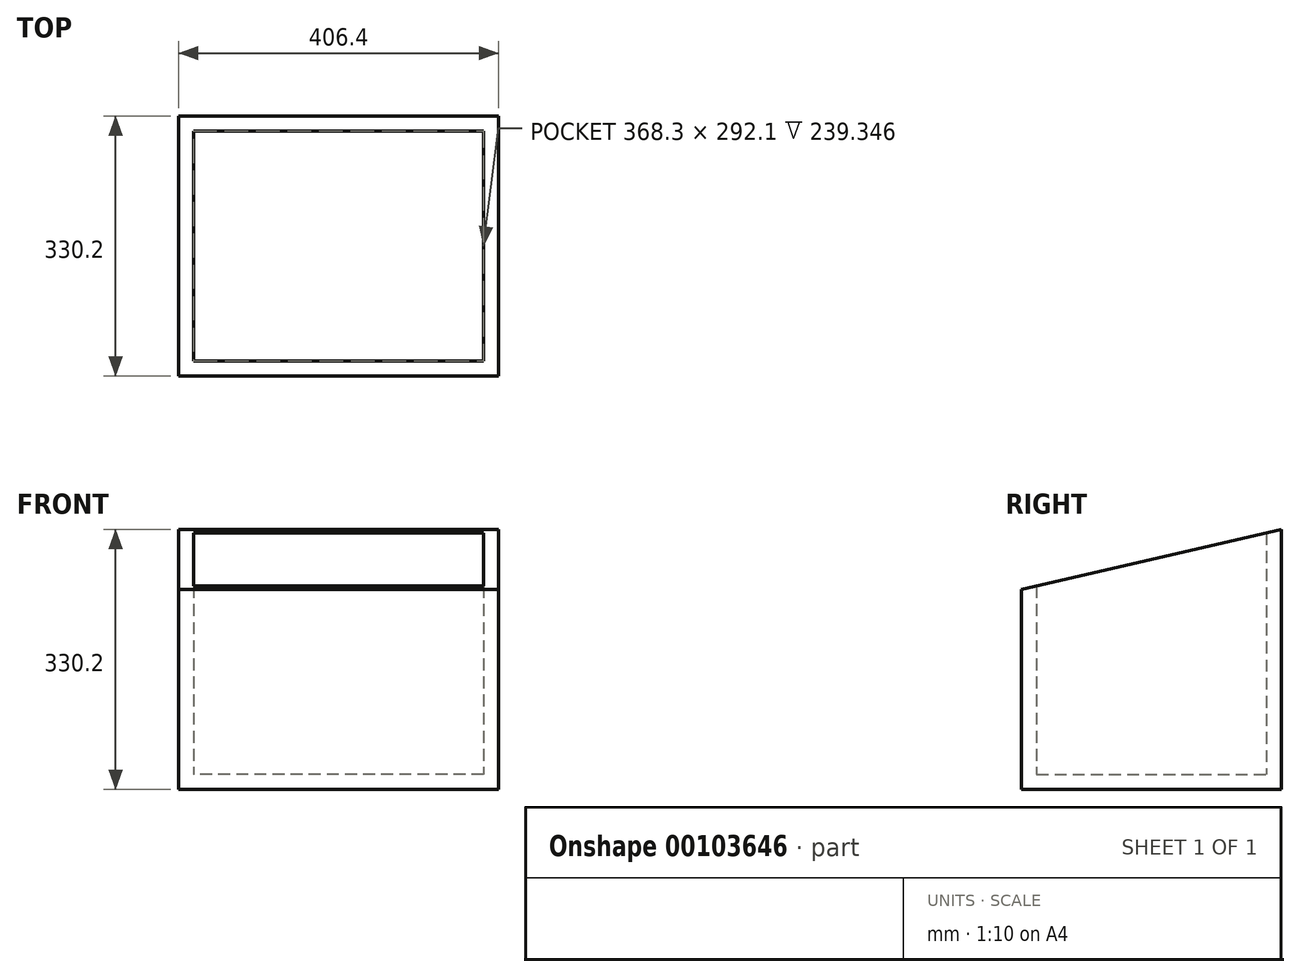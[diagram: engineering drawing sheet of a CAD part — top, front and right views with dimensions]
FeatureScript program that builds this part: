
annotation { "Feature Type Name" : "Feature", "Feature Type Description" : "" }
export const myFeature = defineFeature(function(context is Context, id is Id, definition is map)
    precondition{}
    {
        {
            var Q0;
            Q0=qCreatedBy(makeId("Front.planeOp"),FACE);
            var sketch = newSketch(context, id + "F0", { "sketchPlane" : qUnion([Q0])});
            skLineSegment(sketch, "E0.bottom", {"start": v(203.2, 165.1) * mm, "end": v(-203.2, 165.1) * mm});
            skLineSegment(sketch, "E0.top", {"start": v(203.2, -165.1) * mm, "end": v(-203.2, -165.1) * mm});
            skLineSegment(sketch, "E0.left", {"start": v(203.2, 165.1) * mm, "end": v(203.2, -165.1) * mm});
            skLineSegment(sketch, "E0.right", {"start": v(-203.2, 165.1) * mm, "end": v(-203.2, -165.1) * mm});
            skPoint(sketch, "E0.middle", {"position": v(0, 0) * mm});
            skSolve(sketch);
        }
        {
            var Q0;
            Q0=makeQuery(id+"F0.imprint","IMPRINT",FACE,{"disambiguationData":[TD([[makeQuery(id+"F0.imprint","IMPRINT",EDGE,{"derivedFrom":sQuery(id+"F0.wireOp",EDGE,"E0.bottom")}),1.0]])]});
            extrude(context, id + "F1", {"entities" : qUnion([Q0]), "endBound" : BoundingType.SYMMETRIC, "depth" : 330.2 * mm});
        }
        {
            var Q0;
            Q0=makeQuery(id+"F1.opExtrude","SWEPT_FACE",FACE,{"disambiguationData":[OSD([sQuery(id+"F0.wireOp",EDGE,"E0.left")])]});
            var sketch = newSketch(context, id + "F2", { "sketchPlane" : qUnion([Q0])});
            skLineSegment(sketch, "E1", {"start": v(-165.1, 165.1) * mm, "end": v(-165.1, 88.9) * mm});
            skLineSegment(sketch, "E2", {"start": v(-165.1, 88.9) * mm, "end": v(165.1, 165.1) * mm});
            skLineSegment(sketch, "E3", {"start": v(165.1, 165.1) * mm, "end": v(-165.1, 165.1) * mm});
            skSolve(sketch);
        }
        {
            var Q0;
            Q0=makeQuery(id+"F2.imprint","IMPRINT",FACE,{"disambiguationData":[TD([[makeQuery(id+"F2.imprint","IMPRINT",EDGE,{"derivedFrom":sQuery(id+"F2.wireOp",EDGE,"E1")}),1.0]])]});
            extrude(context, id + "F3", {"entities" : qUnion([Q0]), "operationType" : NewBodyOperationType.REMOVE, "endBound" : BoundingType.THROUGH_ALL, "oppositeDirection" : true, "depth" : 25.4 * mm});
        }
        {
            var Q0;
            Q0=makeQuery(id+"F3.boolean.opBoolean","COPY",FACE,{"derivedFrom":makeQuery(id+"F3.opExtrude","SWEPT_FACE",FACE,{"disambiguationData":[OSD([sQuery(id+"F2.wireOp",EDGE,"E2")])]})});
            shell(context, id + "F4", {"entities" : qUnion([Q0]), "thickness" : 19.05 * mm});
        }
    });
